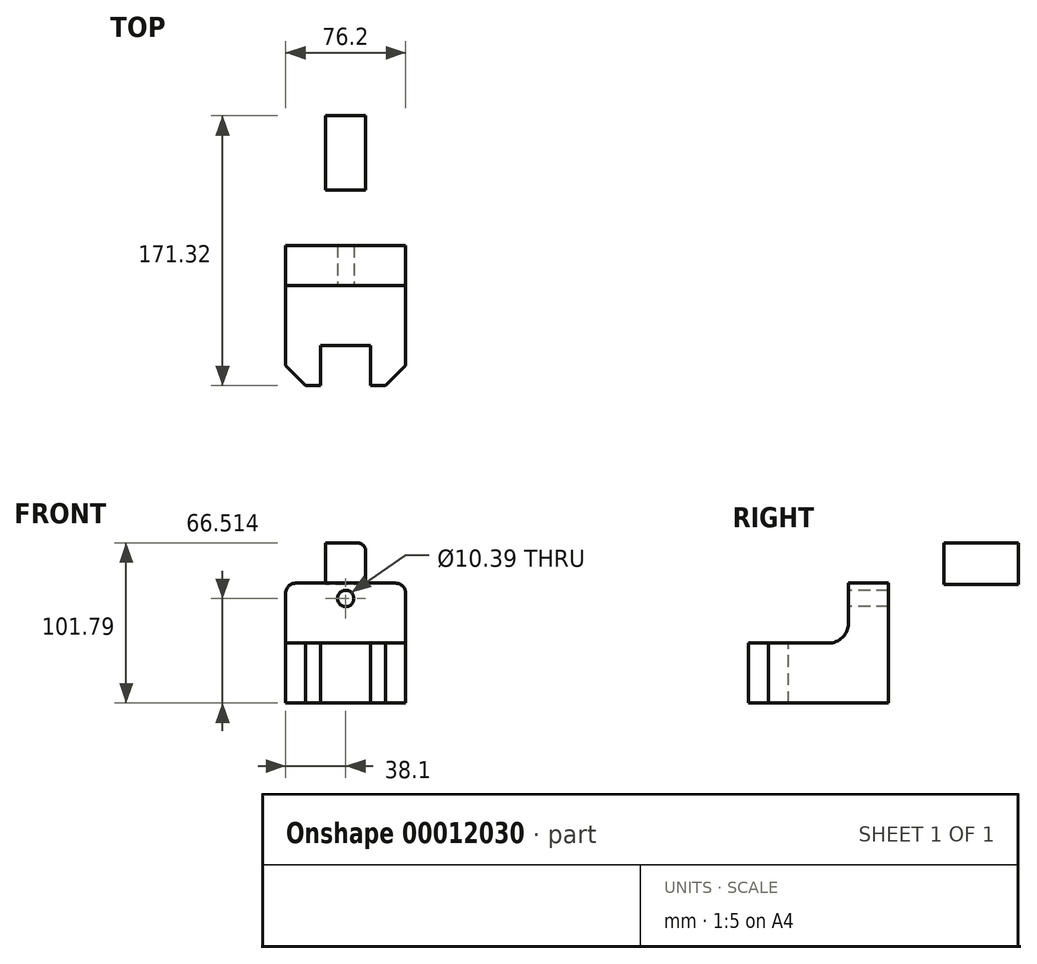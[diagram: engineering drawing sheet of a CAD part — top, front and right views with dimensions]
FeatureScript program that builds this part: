
annotation { "Feature Type Name" : "Feature", "Feature Type Description" : "" }
export const myFeature = defineFeature(function(context is Context, id is Id, definition is map)
    precondition{}
    {
        {
            var Q0;
            Q0=qCreatedBy(makeId("Front.planeOp"),FACE);
            var sketch = newSketch(context, id + "F0", { "sketchPlane" : qUnion([Q0])});
            skLineSegment(sketch, "E0.rect.bottom", {"start": v(76.2, 38.1) * mm, "end": v(-76.2, 38.1) * mm});
            skLineSegment(sketch, "E0.rect.top", {"start": v(76.2, -38.1) * mm, "end": v(-76.2, -38.1) * mm});
            skLineSegment(sketch, "E0.rect.left", {"start": v(76.2, 38.1) * mm, "end": v(76.2, -38.1) * mm});
            skLineSegment(sketch, "E0.rect.right", {"start": v(-76.2, 38.1) * mm, "end": v(-76.2, -38.1) * mm});
            skPoint(sketch, "E0.rect.middle", {"position": v(0, 0) * mm});
            skSolve(sketch);
        }
        {
            var Q0;
            Q0 = qSketchRegion(id + "F0", true);
            extrude(context, id + "F1", {"entities" : qUnion([Q0]), "depth" : 127 * mm});
        }
        {
            var Q0;
            Q0=makeQuery(id+"F1.opExtrude","CAP_FACE",FACE,{"disambiguationData":[OSD([sQuery(id+"F0.wireOp",EDGE,"E0.rect.bottom"),sQuery(id+"F0.wireOp",EDGE,"E0.rect.top"),sQuery(id+"F0.wireOp",EDGE,"E0.rect.left"),sQuery(id+"F0.wireOp",EDGE,"E0.rect.right")])],"isStart":false});
            var sketch = newSketch(context, id + "F2", { "sketchPlane" : qUnion([Q0])});
            skLineSegment(sketch, "E1.rect.bottom", {"start": v(25.4, 12.7) * mm, "end": v(-25.4, 12.7) * mm});
            skLineSegment(sketch, "E1.rect.top", {"start": v(25.4, -12.7) * mm, "end": v(-25.4, -12.7) * mm});
            skLineSegment(sketch, "E1.rect.left", {"start": v(25.4, 12.7) * mm, "end": v(25.4, -12.7) * mm});
            skLineSegment(sketch, "E1.rect.right", {"start": v(-25.4, 12.7) * mm, "end": v(-25.4, -12.7) * mm});
            skPoint(sketch, "E1.rect.middle", {"position": v(0, 0) * mm});
            skSolve(sketch);
        }
        {
            var Q0;
            Q0 = qSketchRegion(id + "F2", true);
            extrude(context, id + "F3", {"entities" : qUnion([Q0]), "operationType" : NewBodyOperationType.REMOVE, "oppositeDirection" : true, "depth" : 76.2 * mm});
        }
        {
            var Q0;
            Q0=makeQuery(id+"F3.boolean.opBoolean","COPY",EDGE,{"derivedFrom":makeQuery(id+"F3.opExtrude","SWEPT_EDGE",EDGE,{"disambiguationData":[OSD([sQuery(id+"F2.wireOp",EDGE,"E1.rect.bottom"),sQuery(id+"F2.wireOp",EDGE,"E1.rect.right")])]})});
            var Q1;
            Q1=makeQuery(id+"F3.boolean.opBoolean","COPY",EDGE,{"derivedFrom":makeQuery(id+"F3.opExtrude","CAP_EDGE",EDGE,{"disambiguationData":[OSD([sQuery(id+"F2.wireOp",EDGE,"E1.rect.bottom")])],"isStart":false})});
            var Q2;
            Q2=makeQuery(id+"F3.boolean.opBoolean","COPY",EDGE,{"derivedFrom":makeQuery(id+"F3.opExtrude","SWEPT_EDGE",EDGE,{"disambiguationData":[OSD([sQuery(id+"F2.wireOp",EDGE,"E1.rect.bottom"),sQuery(id+"F2.wireOp",EDGE,"E1.rect.left")])]})});
            var Q3;
            Q3=makeQuery(id+"F3.boolean.opBoolean","COPY",EDGE,{"derivedFrom":makeQuery(id+"F3.opExtrude","SWEPT_EDGE",EDGE,{"disambiguationData":[OSD([sQuery(id+"F2.wireOp",EDGE,"E1.rect.top"),sQuery(id+"F2.wireOp",EDGE,"E1.rect.left")])]})});
            var Q4;
            Q4=makeQuery(id+"F3.boolean.opBoolean","COPY",EDGE,{"derivedFrom":makeQuery(id+"F3.opExtrude","CAP_EDGE",EDGE,{"disambiguationData":[OSD([sQuery(id+"F2.wireOp",EDGE,"E1.rect.top")])],"isStart":false})});
            var Q5;
            Q5=makeQuery(id+"F3.boolean.opBoolean","COPY",EDGE,{"derivedFrom":makeQuery(id+"F3.opExtrude","SWEPT_EDGE",EDGE,{"disambiguationData":[OSD([sQuery(id+"F2.wireOp",EDGE,"E1.rect.top"),sQuery(id+"F2.wireOp",EDGE,"E1.rect.right")])]})});
            var Q6;
            Q6=makeQuery(id+"F3.boolean.opBoolean","COPY",EDGE,{"derivedFrom":makeQuery(id+"F3.opExtrude","CAP_EDGE",EDGE,{"disambiguationData":[OSD([sQuery(id+"F2.wireOp",EDGE,"E1.rect.left")])],"isStart":false})});
            var Q7;
            Q7=makeQuery(id+"F3.boolean.opBoolean","COPY",EDGE,{"derivedFrom":makeQuery(id+"F3.opExtrude","CAP_EDGE",EDGE,{"disambiguationData":[OSD([sQuery(id+"F2.wireOp",EDGE,"E1.rect.left")])],"isStart":true})});
            var Q8;
            Q8=makeQuery(id+"F3.boolean.opBoolean","COPY",EDGE,{"derivedFrom":makeQuery(id+"F3.opExtrude","CAP_EDGE",EDGE,{"disambiguationData":[OSD([sQuery(id+"F2.wireOp",EDGE,"E1.rect.right")])],"isStart":false})});
            fillet(context, id + "F4", {"entities" : qUnion([Q0, Q1, Q2, Q3, Q4, Q5, Q6, Q7, Q8]), "radius" : 6.35 * mm, "tangentPropagation" : true, "allowEdgeOverflow" : false});
        }
        {
            var Q0;
            Q0=qCreatedBy(makeId("Front.planeOp"),FACE);
            var sketch = newSketch(context, id + "F5", { "sketchPlane" : qUnion([Q0])});
            skLineSegment(sketch, "E2.rect.bottom", {"start": v(38.1, 38.1) * mm, "end": v(-38.1, 38.1) * mm});
            skLineSegment(sketch, "E2.rect.top", {"start": v(38.1, -38.1) * mm, "end": v(-38.1, -38.1) * mm});
            skLineSegment(sketch, "E2.rect.left", {"start": v(38.1, 38.1) * mm, "end": v(38.1, -38.1) * mm});
            skLineSegment(sketch, "E2.rect.right", {"start": v(-38.1, 38.1) * mm, "end": v(-38.1, -38.1) * mm});
            skPoint(sketch, "E2.rect.middle", {"position": v(0, 0) * mm});
            skSolve(sketch);
        }
        {
            var Q0;
            Q0=makeQuery(id+"F5.imprint","IMPRINT",FACE,{"disambiguationData":[TD([[makeQuery(id+"F5.imprint","IMPRINT",EDGE,{"derivedFrom":sQuery(id+"F5.wireOp",EDGE,"E2.rect.bottom")}),1.0]])]});
            extrude(context, id + "F6", {"entities" : qUnion([Q0]), "depth" : 88.9 * mm});
        }
        {
            var Q0;
            Q0=makeQuery(id+"F6.opExtrude","SWEPT_FACE",FACE,{"disambiguationData":[OSD([sQuery(id+"F5.wireOp",EDGE,"E2.rect.left")])]});
            var sketch = newSketch(context, id + "F7", { "sketchPlane" : qUnion([Q0])});
            skLineSegment(sketch, "E3.bottom", {"start": v(-88.9, 38.1) * mm, "end": v(-25.4, 38.1) * mm});
            skLineSegment(sketch, "E3.top", {"start": v(-88.9, 0) * mm, "end": v(-25.4, 0) * mm});
            skLineSegment(sketch, "E3.left", {"start": v(-88.9, 38.1) * mm, "end": v(-88.9, 0) * mm});
            skLineSegment(sketch, "E3.right", {"start": v(-25.4, 38.1) * mm, "end": v(-25.4, 0) * mm});
            skSolve(sketch);
        }
        {
            var Q0;
            Q0=makeQuery(id+"F7.imprint","IMPRINT",FACE,{"disambiguationData":[TD([[makeQuery(id+"F7.imprint","IMPRINT",EDGE,{"derivedFrom":sQuery(id+"F7.wireOp",EDGE,"E3.bottom")}),-1.0]])]});
            extrude(context, id + "F8", {"entities" : qUnion([Q0]), "operationType" : NewBodyOperationType.REMOVE, "endBound" : BoundingType.UP_TO_NEXT, "oppositeDirection" : true, "depth" : 25.4 * mm});
        }
        {
            var Q0;
            Q0=makeQuery(id+"F6.opExtrude","CAP_EDGE",EDGE,{"disambiguationData":[OSD([sQuery(id+"F5.wireOp",EDGE,"E2.rect.left")])],"isStart":false});
            var Q1;
            Q1=makeQuery(id+"F6.opExtrude","CAP_EDGE",EDGE,{"disambiguationData":[OSD([sQuery(id+"F5.wireOp",EDGE,"E2.rect.right")])],"isStart":false});
            chamfer(context, id + "F9", {"entities" : qUnion([Q0, Q1]), "width" : 12.7 * mm, "tangentPropagation" : true});
        }
        {
            var Q0;
            Q0=makeQuery(id+"F6.opExtrude","SWEPT_EDGE",EDGE,{"disambiguationData":[OSD([sQuery(id+"F5.wireOp",EDGE,"E2.rect.bottom"),sQuery(id+"F5.wireOp",EDGE,"E2.rect.left")])]});
            var Q1;
            Q1=makeQuery(id+"F6.opExtrude","SWEPT_EDGE",EDGE,{"disambiguationData":[OSD([sQuery(id+"F5.wireOp",EDGE,"E2.rect.bottom"),sQuery(id+"F5.wireOp",EDGE,"E2.rect.right")])]});
            fillet(context, id + "F10", {"entities" : qUnion([Q0, Q1]), "radius" : 6.35 * mm, "tangentPropagation" : true, "allowEdgeOverflow" : false});
        }
        {
            var Q0;
            Q0=makeQuery(id+"F8.boolean.opBoolean","COPY",FACE,{"disambiguationData":[OD(0.0)],"derivedFrom":makeQuery(id+"F8.opExtrude","SWEPT_FACE",FACE,{"disambiguationData":[OSD([sQuery(id+"F7.wireOp",EDGE,"E3.top")])]})});
            var sketch = newSketch(context, id + "F11", { "sketchPlane" : qUnion([Q0])});
            skLineSegment(sketch, "E4.rect.bottom", {"start": v(15.88, -63.5) * mm, "end": v(-15.87, -63.5) * mm});
            skLineSegment(sketch, "E4.rect.top", {"start": v(15.88, -114.3) * mm, "end": v(-15.87, -114.3) * mm});
            skLineSegment(sketch, "E4.rect.left", {"start": v(15.88, -63.5) * mm, "end": v(15.88, -114.3) * mm});
            skLineSegment(sketch, "E4.rect.right", {"start": v(-15.87, -63.5) * mm, "end": v(-15.87, -114.3) * mm});
            skPoint(sketch, "E4.rect.middle", {"position": v(0, -88.9) * mm});
            skSolve(sketch);
        }
        {
            var Q0;
            {var subQ5=sQuery(id+"F11.wireOp",EDGE,"E4.rect.bottom");Q0=makeQuery(id+"F11.imprint","IMPRINT",FACE,{"disambiguationData":[TD([[makeQuery(id+"F11.imprint","IMPRINT",EDGE,{"derivedFrom":subQ5}),1.0]])]});}
            extrude(context, id + "F12", {"entities" : qUnion([Q0]), "operationType" : NewBodyOperationType.REMOVE, "endBound" : BoundingType.THROUGH_ALL, "oppositeDirection" : true, "depth" : 25.4 * mm});
        }
        {
            var Q0;
            Q0=makeQuery(id+"F8.boolean.opBoolean","COPY",EDGE,{"disambiguationData":[OD(1.0)],"derivedFrom":makeQuery(id+"F8.opExtrude","SWEPT_EDGE",EDGE,{"disambiguationData":[OSD([sQuery(id+"F7.wireOp",EDGE,"E3.top"),sQuery(id+"F7.wireOp",EDGE,"E3.right")])]})});
            fillet(context, id + "F13", {"entities" : qUnion([Q0]), "radius" : 12.7 * mm, "tangentPropagation" : true, "allowEdgeOverflow" : false});
        }
        {
            var Q0;
            Q0=makeQuery(id+"F8.boolean.opBoolean","COPY",FACE,{"disambiguationData":[OD(1.0)],"derivedFrom":makeQuery(id+"F8.opExtrude","SWEPT_FACE",FACE,{"disambiguationData":[OSD([sQuery(id+"F7.wireOp",EDGE,"E3.right")])]})});
            var sketch = newSketch(context, id + "F14", { "sketchPlane" : qUnion([Q0])});
            skCircle(sketch, "E5", {"center": v(-34.95, 42.48) * mm, "radius": 1.57 * mm});
            skCircle(sketch, "E6", {"center": v(0, 28.41) * mm, "radius": 5.2 * mm});
            skSolve(sketch);
        }
        {
            var Q0;
            Q0=makeQuery(id+"F14.imprint","IMPRINT",FACE,{"disambiguationData":[TD([[makeQuery(id+"F14.imprint","IMPRINT",EDGE,{"derivedFrom":sQuery(id+"F14.wireOp",EDGE,"E6")}),1.0]])]});
            extrude(context, id + "F15", {"entities" : qUnion([Q0]), "operationType" : NewBodyOperationType.REMOVE, "oppositeDirection" : true, "depth" : 25.4 * mm});
        }
        {
            var Q0;
            Q0=makeQuery(id+"F1.opExtrude","SWEPT_BODY",BODY,{"disambiguationData":[OSD([sQuery(id+"F0.wireOp",EDGE,"E0.rect.bottom"),sQuery(id+"F0.wireOp",EDGE,"E0.rect.top"),sQuery(id+"F0.wireOp",EDGE,"E0.rect.left"),sQuery(id+"F0.wireOp",EDGE,"E0.rect.right")])]});
            deleteBodies(context, id + "F16", {"entities" : qUnion([Q0])});
        }
        {
            var Q0;
            Q0=qCreatedBy(makeId("Right.planeOp"),FACE);
            var sketch = newSketch(context, id + "F17", { "sketchPlane" : qUnion([Q0])});
            skLineSegment(sketch, "E7.rect.bottom", {"start": v(82.42, 37.3) * mm, "end": v(35.16, 37.3) * mm});
            skLineSegment(sketch, "E7.rect.top", {"start": v(82.42, 63.69) * mm, "end": v(35.16, 63.69) * mm});
            skLineSegment(sketch, "E7.rect.left", {"start": v(82.42, 37.3) * mm, "end": v(82.42, 63.69) * mm});
            skLineSegment(sketch, "E7.rect.right", {"start": v(35.16, 37.3) * mm, "end": v(35.16, 63.69) * mm});
            skPoint(sketch, "E7.rect.middle", {"position": v(58.8, 50.5) * mm});
            skSolve(sketch);
        }
        {
            var Q0;
            Q0=makeQuery(id+"F17.imprint","IMPRINT",FACE,{"disambiguationData":[TD([[makeQuery(id+"F17.imprint","IMPRINT",EDGE,{"derivedFrom":sQuery(id+"F17.wireOp",EDGE,"E7.rect.bottom")}),-1.0]])]});
            extrude(context, id + "F18", {"entities" : qUnion([Q0]), "endBound" : BoundingType.SYMMETRIC, "depth" : 25.4 * mm});
        }
        {
            var Q0;
            Q0=makeQuery(id+"F18.opExtrude","CAP_EDGE",EDGE,{"disambiguationData":[OSD([sQuery(id+"F17.wireOp",EDGE,"E7.rect.top")])],"isStart":false});
            fillet(context, id + "F19", {"entities" : qUnion([Q0]), "radius" : 5.08 * mm, "tangentPropagation" : true, "allowEdgeOverflow" : false});
        }
    });
